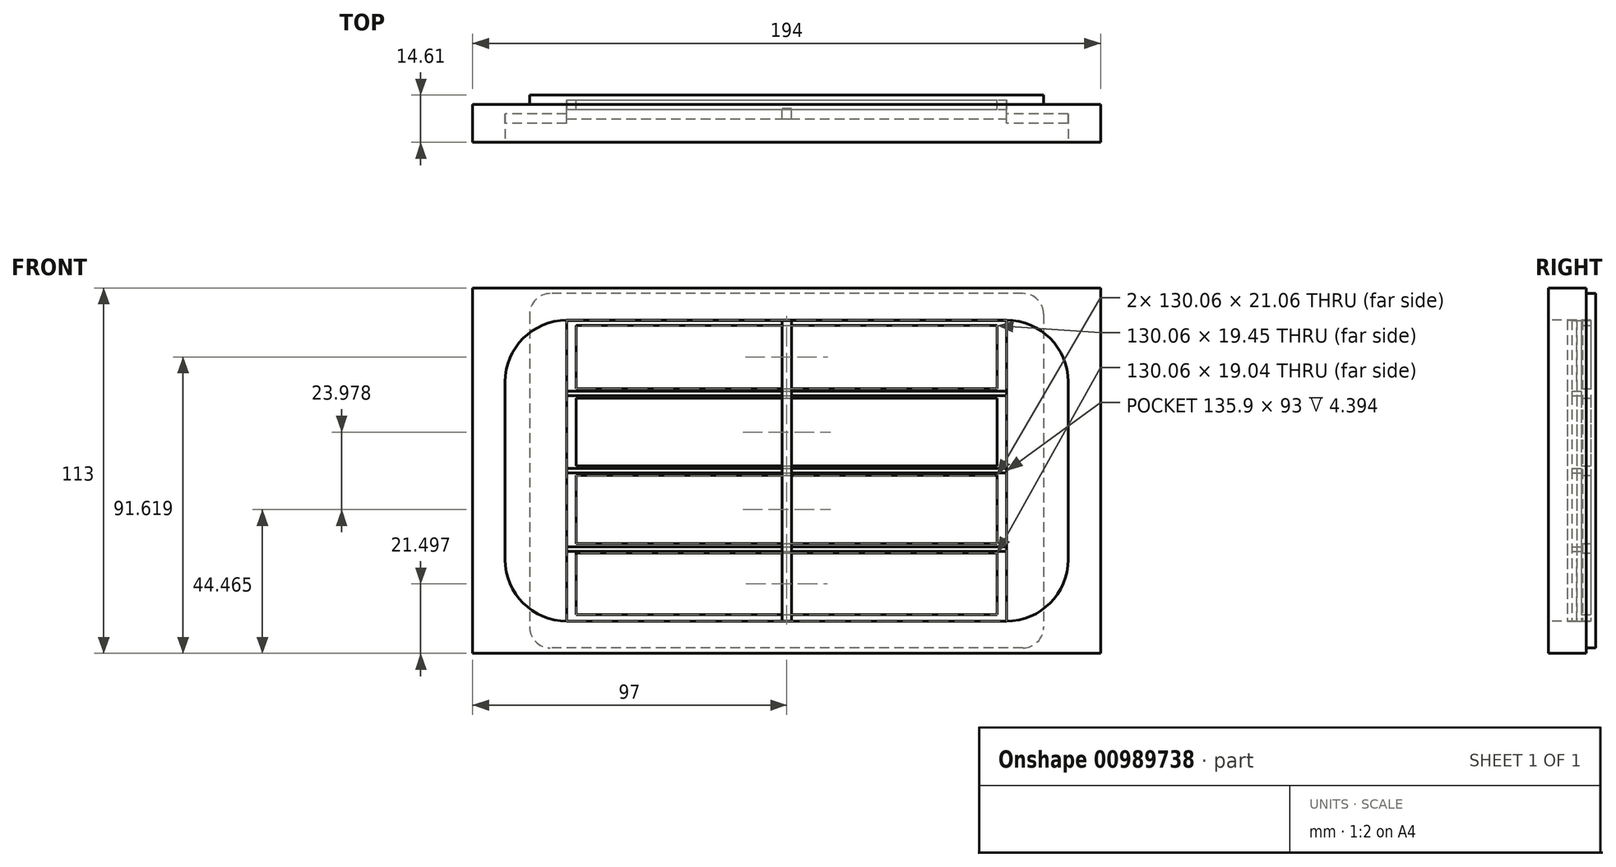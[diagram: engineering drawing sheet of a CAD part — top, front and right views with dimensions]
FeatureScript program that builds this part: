
annotation { "Feature Type Name" : "Feature", "Feature Type Description" : "" }
export const myFeature = defineFeature(function(context is Context, id is Id, definition is map)
    precondition{}
    {
        {
            var Q0;
            Q0=qCreatedBy(makeId("Front.planeOp"),FACE);
            var sketch = newSketch(context, id + "F0", { "sketchPlane" : qUnion([Q0])});
            skLineSegment(sketch, "E0.bottom", {"start": v(73.03, 54.77) * mm, "end": v(-73.03, 54.77) * mm});
            skLineSegment(sketch, "E0.top", {"start": v(73.03, -54.77) * mm, "end": v(-73.02, -54.77) * mm});
            skLineSegment(sketch, "E0.left", {"start": v(79.38, 48.42) * mm, "end": v(79.38, -48.42) * mm});
            skLineSegment(sketch, "E0.right", {"start": v(-79.38, 48.42) * mm, "end": v(-79.37, -48.42) * mm});
            skPoint(sketch, "E0.middle", {"position": v(0, 0) * mm});
            skPoint(sketch, "E1.visualSharp", {"position": v(-79.37, -54.77) * mm});
            skArc(sketch, "E1.filletArc", {"start": v(-79.37, -48.42) * mm, "mid": v(-77.52, -52.9) * mm, "end": v(-73.02, -54.77) * mm});
            skPoint(sketch, "E2.visualSharp", {"position": v(79.38, -54.77) * mm});
            skArc(sketch, "E2.filletArc", {"start": v(73.03, -54.77) * mm, "mid": v(77.52, -52.9) * mm, "end": v(79.38, -48.42) * mm});
            skPoint(sketch, "E3.visualSharp", {"position": v(79.38, 54.77) * mm});
            skArc(sketch, "E3.filletArc", {"start": v(79.38, 48.42) * mm, "mid": v(77.52, 52.9) * mm, "end": v(73.03, 54.77) * mm});
            skPoint(sketch, "E4.visualSharp", {"position": v(-79.38, 54.77) * mm});
            skArc(sketch, "E4.filletArc", {"start": v(-73.03, 54.77) * mm, "mid": v(-77.52, 52.9) * mm, "end": v(-79.38, 48.42) * mm});
            skSolve(sketch);
        }
        {
            var Q0;
            Q0=qSketchRegion(id+"F0",true);
            extrude(context, id + "F1", {"entities" : qUnion([Q0]), "depth" : 2.92 * mm, "offsetDistance" : 25.4 * mm});
        }
        {
            var Q0;
            Q0=makeQuery(id+"F1.opExtrude","CAP_FACE",FACE,{"disambiguationData":[OSD([sQuery(id+"F0.wireOp",EDGE,"E0.bottom"),sQuery(id+"F0.wireOp",EDGE,"E0.top"),sQuery(id+"F0.wireOp",EDGE,"E0.left"),sQuery(id+"F0.wireOp",EDGE,"E0.right")])],"isStart":false});
            var sketch = newSketch(context, id + "F2", { "sketchPlane" : qUnion([Q0])});
            skLineSegment(sketch, "E5.bottom", {"start": v(-97, 56.5) * mm, "end": v(97, 56.5) * mm});
            skLineSegment(sketch, "E5.top", {"start": v(-97, -56.5) * mm, "end": v(97, -56.5) * mm});
            skLineSegment(sketch, "E5.left", {"start": v(-97, 56.5) * mm, "end": v(-97, -56.5) * mm});
            skLineSegment(sketch, "E5.right", {"start": v(97, 56.5) * mm, "end": v(97, -56.5) * mm});
            skPoint(sketch, "E5.middle", {"position": v(0, 0) * mm});
            skSolve(sketch);
        }
        {
            var Q0;
            Q0=qSketchRegion(id+"F2",true);
            extrude(context, id + "F3", {"entities" : qUnion([Q0]), "operationType" : NewBodyOperationType.ADD, "depth" : 11.68 * mm, "offsetDistance" : 25.4 * mm});
        }
        {
            var Q0;
            Q0=makeQuery(id+"F3.opExtrude","CAP_FACE",FACE,{"disambiguationData":[OSD([sQuery(id+"F2.wireOp",EDGE,"E5.bottom"),sQuery(id+"F2.wireOp",EDGE,"E5.top"),sQuery(id+"F2.wireOp",EDGE,"E5.left"),sQuery(id+"F2.wireOp",EDGE,"E5.right")])],"isStart":false});
            var sketch = newSketch(context, id + "F4", { "sketchPlane" : qUnion([Q0])});
            skLineSegment(sketch, "E6.bottom", {"start": v(-67.95, 46.5) * mm, "end": v(67.95, 46.5) * mm});
            skLineSegment(sketch, "E6.top", {"start": v(-67.95, -46.5) * mm, "end": v(67.95, -46.5) * mm});
            skLineSegment(sketch, "E6.left", {"start": v(-87, 27.45) * mm, "end": v(-87, -27.45) * mm});
            skLineSegment(sketch, "E6.right", {"start": v(87, 27.45) * mm, "end": v(87, -27.45) * mm});
            skPoint(sketch, "E6.middle", {"position": v(0, 0) * mm});
            skPoint(sketch, "E7.visualSharp", {"position": v(-87, 46.5) * mm});
            skArc(sketch, "E7.filletArc", {"start": v(-67.95, 46.5) * mm, "mid": v(-81.42, 40.92) * mm, "end": v(-87, 27.45) * mm});
            skPoint(sketch, "E8.visualSharp", {"position": v(87, 46.5) * mm});
            skArc(sketch, "E8.filletArc", {"start": v(87, 27.45) * mm, "mid": v(81.42, 40.92) * mm, "end": v(67.95, 46.5) * mm});
            skPoint(sketch, "E9.visualSharp", {"position": v(87, -46.5) * mm});
            skArc(sketch, "E9.filletArc", {"start": v(67.95, -46.5) * mm, "mid": v(81.42, -40.92) * mm, "end": v(87, -27.45) * mm});
            skPoint(sketch, "E10.visualSharp", {"position": v(-87, -46.5) * mm});
            skArc(sketch, "E10.filletArc", {"start": v(-87, -27.45) * mm, "mid": v(-81.42, -40.92) * mm, "end": v(-67.95, -46.5) * mm});
            skSolve(sketch);
        }
        {
            var Q0;
            Q0=makeQuery(id+"F4.imprint","IMPRINT",FACE,{"disambiguationData":[TD([[makeQuery(id+"F4.imprint","IMPRINT",EDGE,{"derivedFrom":sQuery(id+"F4.wireOp",EDGE,"E6.bottom")}),-1.0]])]});
            extrude(context, id + "F5", {"entities" : qUnion([Q0]), "operationType" : NewBodyOperationType.REMOVE, "oppositeDirection" : true, "depth" : 8.76 * mm, "offsetDistance" : 25.4 * mm});
        }
        {
            var Q0;
            Q0=makeQuery(id+"F5.boolean.opBoolean","COPY",FACE,{"derivedFrom":makeQuery(id+"F5.opExtrude","CAP_FACE",FACE,{"disambiguationData":[OSD([sQuery(id+"F4.wireOp",EDGE,"E6.bottom"),sQuery(id+"F4.wireOp",EDGE,"E6.top"),sQuery(id+"F4.wireOp",EDGE,"E6.left"),sQuery(id+"F4.wireOp",EDGE,"E6.right"),sQuery(id+"F4.wireOp",EDGE,"E7.filletArc"),sQuery(id+"F4.wireOp",EDGE,"E8.filletArc"),sQuery(id+"F4.wireOp",EDGE,"E9.filletArc"),sQuery(id+"F4.wireOp",EDGE,"E10.filletArc")])],"isStart":false})});
            var sketch = newSketch(context, id + "F6", { "sketchPlane" : qUnion([Q0])});
            skLineSegment(sketch, "E11.bottom", {"start": v(-67.95, 46.5) * mm, "end": v(67.95, 46.5) * mm});
            skLineSegment(sketch, "E11.top", {"start": v(-67.95, -46.5) * mm, "end": v(67.95, -46.5) * mm});
            skLineSegment(sketch, "E11.left", {"start": v(-67.95, 46.5) * mm, "end": v(-67.95, -46.5) * mm});
            skLineSegment(sketch, "E11.right", {"start": v(67.95, 46.5) * mm, "end": v(67.95, -46.5) * mm});
            skSolve(sketch);
        }
        {
            var Q0;
            Q0=makeQuery(id+"F6.imprint","IMPRINT",FACE,{"disambiguationData":[TD([[makeQuery(id+"F6.imprint","IMPRINT",EDGE,{"derivedFrom":sQuery(id+"F6.wireOp",EDGE,"E11.bottom")}),-1.0]])]});
            extrude(context, id + "F7", {"entities" : qUnion([Q0]), "operationType" : NewBodyOperationType.REMOVE, "oppositeDirection" : true, "depth" : 4.4 * mm, "offsetDistance" : 25.4 * mm});
        }
        {
            var Q0;
            Q0=qCreatedBy(makeId("Front.planeOp"),FACE);
            cPlane(context, id + "F8", {"entities" : qUnion([Q0]), "cplaneType" : CPlaneType.OFFSET, "offset" : 4 * mm, "width" : 152.4 * mm, "height" : 152.4 * mm});
        }
        {
            var Q0;
            Q0=qCreatedBy(id+"F8.planeOp",FACE);
            var sketch = newSketch(context, id + "F9", { "sketchPlane" : qUnion([Q0])});
            skLineSegment(sketch, "E12.bottom", {"start": v(-1.46, 46.45) * mm, "end": v(1.46, 46.45) * mm});
            skLineSegment(sketch, "E12.top", {"start": v(-1.46, -46.55) * mm, "end": v(1.46, -46.55) * mm});
            skLineSegment(sketch, "E12.left", {"start": v(-1.46, 46.45) * mm, "end": v(-1.46, -46.55) * mm});
            skLineSegment(sketch, "E12.right", {"start": v(1.46, 46.45) * mm, "end": v(1.46, -46.55) * mm});
            skPoint(sketch, "E12.middle", {"position": v(0, -0.05) * mm});
            skLineSegment(sketch, "E13.bottom", {"start": v(-67.95, 46.45) * mm, "end": v(-65.03, 46.45) * mm});
            skLineSegment(sketch, "E13.top", {"start": v(-67.95, -46.55) * mm, "end": v(-65.03, -46.55) * mm});
            skLineSegment(sketch, "E13.left", {"start": v(-67.95, 46.45) * mm, "end": v(-67.95, -46.55) * mm});
            skLineSegment(sketch, "E13.right", {"start": v(-65.03, 46.45) * mm, "end": v(-65.03, -46.55) * mm});
            skLineSegment(sketch, "E14.bottom", {"start": v(67.95, 47.77) * mm, "end": v(65.03, 47.77) * mm});
            skLineSegment(sketch, "E14.top", {"start": v(67.95, -47.44) * mm, "end": v(65.03, -47.44) * mm});
            skLineSegment(sketch, "E14.left", {"start": v(67.95, 47.77) * mm, "end": v(67.95, -47.44) * mm});
            skLineSegment(sketch, "E14.right", {"start": v(65.03, 47.77) * mm, "end": v(65.03, -47.44) * mm});
            skLineSegment(sketch, "E15.bottom", {"start": v(-65.03, 1.41) * mm, "end": v(65.03, 1.41) * mm});
            skLineSegment(sketch, "E15.top", {"start": v(-65.03, -1.5) * mm, "end": v(65.03, -1.5) * mm});
            skLineSegment(sketch, "E15.left", {"start": v(-65.03, 1.41) * mm, "end": v(-65.03, -1.5) * mm});
            skLineSegment(sketch, "E15.right", {"start": v(65.03, 1.41) * mm, "end": v(65.03, -1.5) * mm});
            skLineSegment(sketch, "E16.bottom", {"start": v(-65.03, 25.4) * mm, "end": v(65.03, 25.4) * mm});
            skLineSegment(sketch, "E16.top", {"start": v(-65.03, 22.47) * mm, "end": v(65.03, 22.47) * mm});
            skLineSegment(sketch, "E16.left", {"start": v(-65.03, 25.4) * mm, "end": v(-65.03, 22.47) * mm});
            skLineSegment(sketch, "E16.right", {"start": v(65.03, 25.4) * mm, "end": v(65.03, 22.47) * mm});
            skPoint(sketch, "E16.middle", {"position": v(0, 23.93) * mm});
            skLineSegment(sketch, "E17.bottom", {"start": v(-65.03, -25.48) * mm, "end": v(65.03, -25.48) * mm});
            skLineSegment(sketch, "E17.top", {"start": v(-65.03, -22.56) * mm, "end": v(65.03, -22.56) * mm});
            skLineSegment(sketch, "E17.left", {"start": v(-65.03, -25.48) * mm, "end": v(-65.03, -22.56) * mm});
            skLineSegment(sketch, "E17.right", {"start": v(65.03, -25.48) * mm, "end": v(65.03, -22.56) * mm});
            skPoint(sketch, "E17.middle", {"position": v(0, -24.02) * mm});
            skLineSegment(sketch, "E18.bottom", {"start": v(-67.95, -46.55) * mm, "end": v(67.95, -46.55) * mm});
            skLineSegment(sketch, "E18.top", {"start": v(-67.95, -44.52) * mm, "end": v(67.95, -44.52) * mm});
            skLineSegment(sketch, "E18.left", {"start": v(-67.95, -46.55) * mm, "end": v(-67.95, -44.52) * mm});
            skLineSegment(sketch, "E18.right", {"start": v(67.95, -46.55) * mm, "end": v(67.95, -44.52) * mm});
            skLineSegment(sketch, "E19.bottom", {"start": v(-67.95, 46.45) * mm, "end": v(67.95, 46.45) * mm});
            skLineSegment(sketch, "E19.top", {"start": v(-67.95, 44.85) * mm, "end": v(67.95, 44.85) * mm});
            skLineSegment(sketch, "E19.left", {"start": v(-67.95, 46.45) * mm, "end": v(-67.95, 44.85) * mm});
            skLineSegment(sketch, "E19.right", {"start": v(67.95, 46.45) * mm, "end": v(67.95, 44.85) * mm});
            skSolve(sketch);
        }
        {
            var Q0;
            {var subQ0=sQuery(id+"F9.wireOp",EDGE,"E19.top");var subQ1=sQuery(id+"F9.wireOp",EDGE,"E12.left");var subQ2=makeQuery(id+"F9.imprint","INTERSECT",VERTEX,{"derivedFrom":[subQ1,subQ0]});Q0=makeQuery(id+"F9.imprint","IMPRINT",FACE,{"disambiguationData":[TD([[makeQuery(id+"F9.imprint","IMPRINT",EDGE,{"disambiguationData":[TD([[subQ2,-1.0]])],"derivedFrom":subQ1}),1.0]])]});}
            var Q1;
            {var subQ0=sQuery(id+"F9.wireOp",EDGE,"E16.top");var subQ1=sQuery(id+"F9.wireOp",EDGE,"E12.left");var subQ2=makeQuery(id+"F9.imprint","INTERSECT",VERTEX,{"derivedFrom":[subQ1,subQ0]});Q1=makeQuery(id+"F9.imprint","IMPRINT",FACE,{"disambiguationData":[TD([[makeQuery(id+"F9.imprint","IMPRINT",EDGE,{"disambiguationData":[TD([[subQ2,-1.0]])],"derivedFrom":subQ1}),1.0]])]});}
            var Q2;
            {var subQ0=sQuery(id+"F9.wireOp",EDGE,"E15.top");var subQ1=sQuery(id+"F9.wireOp",EDGE,"E12.left");var subQ2=makeQuery(id+"F9.imprint","INTERSECT",VERTEX,{"derivedFrom":[subQ1,subQ0]});Q2=makeQuery(id+"F9.imprint","IMPRINT",FACE,{"disambiguationData":[TD([[makeQuery(id+"F9.imprint","IMPRINT",EDGE,{"disambiguationData":[TD([[subQ2,-1.0]])],"derivedFrom":subQ1}),1.0]])]});}
            var Q3;
            {var subQ0=sQuery(id+"F9.wireOp",EDGE,"E17.bottom");var subQ1=sQuery(id+"F9.wireOp",EDGE,"E12.left");var subQ2=makeQuery(id+"F9.imprint","INTERSECT",VERTEX,{"derivedFrom":[subQ1,subQ0]});Q3=makeQuery(id+"F9.imprint","IMPRINT",FACE,{"disambiguationData":[TD([[makeQuery(id+"F9.imprint","IMPRINT",EDGE,{"disambiguationData":[TD([[subQ2,-1.0]])],"derivedFrom":subQ1}),1.0]])]});}
            var Q4;
            {var subQ0=sQuery(id+"F9.wireOp",EDGE,"E16.bottom");var subQ1=sQuery(id+"F9.wireOp",EDGE,"E12.left");var subQ2=makeQuery(id+"F9.imprint","INTERSECT",VERTEX,{"derivedFrom":[subQ1,subQ0]});Q4=makeQuery(id+"F9.imprint","IMPRINT",FACE,{"disambiguationData":[TD([[makeQuery(id+"F9.imprint","IMPRINT",EDGE,{"disambiguationData":[TD([[subQ2,-1.0]])],"derivedFrom":subQ1}),1.0]])]});}
            var Q5;
            {var subQ0=sQuery(id+"F9.wireOp",EDGE,"E15.bottom");var subQ1=sQuery(id+"F9.wireOp",EDGE,"E12.left");var subQ2=makeQuery(id+"F9.imprint","INTERSECT",VERTEX,{"derivedFrom":[subQ1,subQ0]});Q5=makeQuery(id+"F9.imprint","IMPRINT",FACE,{"disambiguationData":[TD([[makeQuery(id+"F9.imprint","IMPRINT",EDGE,{"disambiguationData":[TD([[subQ2,-1.0]])],"derivedFrom":subQ1}),1.0]])]});}
            var Q6;
            {var subQ0=sQuery(id+"F9.wireOp",EDGE,"E17.top");var subQ1=sQuery(id+"F9.wireOp",EDGE,"E12.left");var subQ2=makeQuery(id+"F9.imprint","INTERSECT",VERTEX,{"derivedFrom":[subQ1,subQ0]});Q6=makeQuery(id+"F9.imprint","IMPRINT",FACE,{"disambiguationData":[TD([[makeQuery(id+"F9.imprint","IMPRINT",EDGE,{"disambiguationData":[TD([[subQ2,-1.0]])],"derivedFrom":subQ1}),1.0]])]});}
            var Q7;
            {var subQ0=sQuery(id+"F9.wireOp",EDGE,"E19.bottom");var subQ1=sQuery(id+"F9.wireOp",EDGE,"E12.left");var subQ2=makeQuery(id+"F9.imprint","INTERSECT",VERTEX,{"derivedFrom":[subQ1,subQ0]});Q7=makeQuery(id+"F9.imprint","IMPRINT",FACE,{"disambiguationData":[TD([[makeQuery(id+"F9.imprint","IMPRINT",EDGE,{"disambiguationData":[TD([[subQ2,-1.0]])],"derivedFrom":subQ1}),1.0]])]});}
            var Q8;
            {var subQ0=sQuery(id+"F9.wireOp",EDGE,"E18.bottom");var subQ1=sQuery(id+"F9.wireOp",EDGE,"E12.left");var subQ2=makeQuery(id+"F9.imprint","INTERSECT",VERTEX,{"derivedFrom":[subQ1,subQ0]});Q8=makeQuery(id+"F9.imprint","IMPRINT",FACE,{"disambiguationData":[TD([[makeQuery(id+"F9.imprint","IMPRINT",EDGE,{"disambiguationData":[TD([[subQ2,1.0]])],"derivedFrom":subQ1}),1.0]])]});}
            extrude(context, id + "F10", {"entities" : qUnion([Q0, Q1, Q2, Q3, Q4, Q5, Q6, Q7, Q8]), "depth" : 3.31 * mm, "offsetDistance" : 25.4 * mm});
        }
        {
            var Q0;
            Q0=makeQuery(id+"F7.boolean.opBoolean","COPY",FACE,{"derivedFrom":makeQuery(id+"F7.opExtrude","CAP_FACE",FACE,{"disambiguationData":[OSD([sQuery(id+"F6.wireOp",EDGE,"E11.bottom"),sQuery(id+"F6.wireOp",EDGE,"E11.top"),sQuery(id+"F6.wireOp",EDGE,"E11.left"),sQuery(id+"F6.wireOp",EDGE,"E11.right")])],"isStart":false})});
            var sketch = newSketch(context, id + "F11", { "sketchPlane" : qUnion([Q0])});
            skLineSegment(sketch, "E20.bottom", {"start": v(-1.46, 46.45) * mm, "end": v(1.46, 46.45) * mm});
            skLineSegment(sketch, "E20.top", {"start": v(-1.46, -46.55) * mm, "end": v(1.46, -46.55) * mm});
            skLineSegment(sketch, "E20.left", {"start": v(-1.46, 46.45) * mm, "end": v(-1.46, -46.55) * mm});
            skLineSegment(sketch, "E20.right", {"start": v(1.46, 46.45) * mm, "end": v(1.46, -46.55) * mm});
            skPoint(sketch, "E20.middle", {"position": v(0, -0.05) * mm});
            skLineSegment(sketch, "E21.bottom", {"start": v(-67.95, 46.45) * mm, "end": v(-65.03, 46.45) * mm});
            skLineSegment(sketch, "E21.top", {"start": v(-67.95, -46.55) * mm, "end": v(-65.03, -46.55) * mm});
            skLineSegment(sketch, "E21.left", {"start": v(-67.95, 46.45) * mm, "end": v(-67.95, -46.55) * mm});
            skLineSegment(sketch, "E21.right", {"start": v(-65.03, 46.45) * mm, "end": v(-65.03, -46.55) * mm});
            skLineSegment(sketch, "E22.bottom", {"start": v(67.95, 47.77) * mm, "end": v(65.03, 47.77) * mm});
            skLineSegment(sketch, "E22.top", {"start": v(67.95, -47.44) * mm, "end": v(65.03, -47.44) * mm});
            skLineSegment(sketch, "E22.left", {"start": v(67.95, 47.77) * mm, "end": v(67.95, -47.44) * mm});
            skLineSegment(sketch, "E22.right", {"start": v(65.03, 47.77) * mm, "end": v(65.03, -47.44) * mm});
            skLineSegment(sketch, "E23.bottom", {"start": v(-65.03, 1.41) * mm, "end": v(65.03, 1.41) * mm});
            skLineSegment(sketch, "E23.top", {"start": v(-65.03, -1.5) * mm, "end": v(65.03, -1.5) * mm});
            skLineSegment(sketch, "E23.left", {"start": v(-65.03, 1.41) * mm, "end": v(-65.03, -1.5) * mm});
            skLineSegment(sketch, "E23.right", {"start": v(65.03, 1.41) * mm, "end": v(65.03, -1.5) * mm});
            skLineSegment(sketch, "E24.bottom", {"start": v(-65.03, 25.4) * mm, "end": v(65.03, 25.4) * mm});
            skLineSegment(sketch, "E24.top", {"start": v(-65.03, 22.47) * mm, "end": v(65.03, 22.47) * mm});
            skLineSegment(sketch, "E24.left", {"start": v(-65.03, 25.4) * mm, "end": v(-65.03, 22.47) * mm});
            skLineSegment(sketch, "E24.right", {"start": v(65.03, 25.4) * mm, "end": v(65.03, 22.47) * mm});
            skPoint(sketch, "E24.middle", {"position": v(0, 23.93) * mm});
            skLineSegment(sketch, "E25.bottom", {"start": v(-65.03, -25.48) * mm, "end": v(65.03, -25.48) * mm});
            skLineSegment(sketch, "E25.top", {"start": v(-65.03, -22.56) * mm, "end": v(65.03, -22.56) * mm});
            skLineSegment(sketch, "E25.left", {"start": v(-65.03, -25.48) * mm, "end": v(-65.03, -22.56) * mm});
            skLineSegment(sketch, "E25.right", {"start": v(65.03, -25.48) * mm, "end": v(65.03, -22.56) * mm});
            skPoint(sketch, "E25.middle", {"position": v(0, -24.02) * mm});
            skLineSegment(sketch, "E26.bottom", {"start": v(-67.95, -46.55) * mm, "end": v(67.95, -46.55) * mm});
            skLineSegment(sketch, "E26.top", {"start": v(-67.95, -44.52) * mm, "end": v(67.95, -44.52) * mm});
            skLineSegment(sketch, "E26.left", {"start": v(-67.95, -46.55) * mm, "end": v(-67.95, -44.52) * mm});
            skLineSegment(sketch, "E26.right", {"start": v(67.95, -46.55) * mm, "end": v(67.95, -44.52) * mm});
            skLineSegment(sketch, "E27.bottom", {"start": v(-67.95, 46.45) * mm, "end": v(67.95, 46.45) * mm});
            skLineSegment(sketch, "E27.top", {"start": v(-67.95, 44.85) * mm, "end": v(67.95, 44.85) * mm});
            skLineSegment(sketch, "E27.left", {"start": v(-67.95, 46.45) * mm, "end": v(-67.95, 44.85) * mm});
            skLineSegment(sketch, "E27.right", {"start": v(67.95, 46.45) * mm, "end": v(67.95, 44.85) * mm});
            skSolve(sketch);
        }
        {
            var Q0;
            {var subQ0=sQuery(id+"F11.wireOp",EDGE,"E24.top");var subQ1=sQuery(id+"F11.wireOp",EDGE,"E20.left");var subQ2=makeQuery(id+"F11.imprint","INTERSECT",VERTEX,{"derivedFrom":[subQ1,subQ0]});Q0=makeQuery(id+"F11.imprint","IMPRINT",FACE,{"disambiguationData":[TD([[makeQuery(id+"F11.imprint","IMPRINT",EDGE,{"disambiguationData":[TD([[subQ2,1.0]])],"derivedFrom":subQ1}),-1.0]])]});}
            var Q1;
            {var subQ0=sQuery(id+"F11.wireOp",EDGE,"E23.bottom");var subQ1=sQuery(id+"F11.wireOp",EDGE,"E20.left");var subQ2=makeQuery(id+"F11.imprint","INTERSECT",VERTEX,{"derivedFrom":[subQ1,subQ0]});Q1=makeQuery(id+"F11.imprint","IMPRINT",FACE,{"disambiguationData":[TD([[makeQuery(id+"F11.imprint","IMPRINT",EDGE,{"disambiguationData":[TD([[subQ2,-1.0]])],"derivedFrom":subQ1}),-1.0]])]});}
            var Q2;
            {var subQ0=sQuery(id+"F11.wireOp",EDGE,"E25.top");var subQ1=sQuery(id+"F11.wireOp",EDGE,"E20.left");var subQ2=makeQuery(id+"F11.imprint","INTERSECT",VERTEX,{"derivedFrom":[subQ1,subQ0]});Q2=makeQuery(id+"F11.imprint","IMPRINT",FACE,{"disambiguationData":[TD([[makeQuery(id+"F11.imprint","IMPRINT",EDGE,{"disambiguationData":[TD([[subQ2,-1.0]])],"derivedFrom":subQ1}),-1.0]])]});}
            var Q3;
            {var subQ0=sQuery(id+"F11.wireOp",EDGE,"E26.top");var subQ1=sQuery(id+"F11.wireOp",EDGE,"E20.left");var subQ2=makeQuery(id+"F11.imprint","INTERSECT",VERTEX,{"derivedFrom":[subQ1,subQ0]});Q3=makeQuery(id+"F11.imprint","IMPRINT",FACE,{"disambiguationData":[TD([[makeQuery(id+"F11.imprint","IMPRINT",EDGE,{"disambiguationData":[TD([[subQ2,-1.0]])],"derivedFrom":subQ1}),-1.0]])]});}
            var Q4;
            {var subQ0=sQuery(id+"F11.wireOp",EDGE,"E21.left");var subQ1=makeQuery(id+"F7.boolean.opBoolean","COPY",EDGE,{"derivedFrom":makeQuery(id+"F7.opExtrude","CAP_EDGE",EDGE,{"disambiguationData":[OSD([sQuery(id+"F6.wireOp",EDGE,"E11.top")])],"isStart":false})});var subQ2=makeQuery(id+"F11.imprint","INTERSECT",VERTEX,{"derivedFrom":[subQ1,subQ0]});Q4=makeQuery(id+"F11.imprint","IMPRINT",FACE,{"disambiguationData":[TD([[makeQuery(id+"F11.imprint","IMPRINT",EDGE,{"disambiguationData":[TD([[subQ2,1.0]])],"derivedFrom":subQ0}),1.0]])]});}
            var Q5;
            {var subQ0=sQuery(id+"F11.wireOp",EDGE,"E26.top");var subQ1=sQuery(id+"F11.wireOp",EDGE,"E20.left");var subQ2=makeQuery(id+"F11.imprint","INTERSECT",VERTEX,{"derivedFrom":[subQ1,subQ0]});Q5=makeQuery(id+"F11.imprint","IMPRINT",FACE,{"disambiguationData":[TD([[makeQuery(id+"F11.imprint","IMPRINT",EDGE,{"disambiguationData":[TD([[subQ2,-1.0]])],"derivedFrom":subQ1}),1.0]])]});}
            var Q6;
            {var subQ0=sQuery(id+"F11.wireOp",EDGE,"E26.top");var subQ1=sQuery(id+"F11.wireOp",EDGE,"E20.right");var subQ2=makeQuery(id+"F11.imprint","INTERSECT",VERTEX,{"derivedFrom":[subQ1,subQ0]});Q6=makeQuery(id+"F11.imprint","IMPRINT",FACE,{"disambiguationData":[TD([[makeQuery(id+"F11.imprint","IMPRINT",EDGE,{"disambiguationData":[TD([[subQ2,-1.0]])],"derivedFrom":subQ1}),1.0]])]});}
            var Q7;
            {var subQ0=sQuery(id+"F11.wireOp",EDGE,"E25.bottom");var subQ1=sQuery(id+"F11.wireOp",EDGE,"E20.right");var subQ2=makeQuery(id+"F11.imprint","INTERSECT",VERTEX,{"derivedFrom":[subQ1,subQ0]});Q7=makeQuery(id+"F11.imprint","IMPRINT",FACE,{"disambiguationData":[TD([[makeQuery(id+"F11.imprint","IMPRINT",EDGE,{"disambiguationData":[TD([[subQ2,1.0]])],"derivedFrom":subQ1}),1.0]])]});}
            var Q8;
            {var subQ0=sQuery(id+"F11.wireOp",EDGE,"E23.bottom");var subQ1=sQuery(id+"F11.wireOp",EDGE,"E20.right");var subQ2=makeQuery(id+"F11.imprint","INTERSECT",VERTEX,{"derivedFrom":[subQ1,subQ0]});Q8=makeQuery(id+"F11.imprint","IMPRINT",FACE,{"disambiguationData":[TD([[makeQuery(id+"F11.imprint","IMPRINT",EDGE,{"disambiguationData":[TD([[subQ2,-1.0]])],"derivedFrom":subQ1}),1.0]])]});}
            var Q9;
            {var subQ0=sQuery(id+"F11.wireOp",EDGE,"E24.top");var subQ1=sQuery(id+"F11.wireOp",EDGE,"E20.right");var subQ2=makeQuery(id+"F11.imprint","INTERSECT",VERTEX,{"derivedFrom":[subQ1,subQ0]});Q9=makeQuery(id+"F11.imprint","IMPRINT",FACE,{"disambiguationData":[TD([[makeQuery(id+"F11.imprint","IMPRINT",EDGE,{"disambiguationData":[TD([[subQ2,1.0]])],"derivedFrom":subQ1}),1.0]])]});}
            var Q10;
            {var subQ4=sQuery(id+"F11.wireOp",EDGE,"E22.left");var subQ10=sQuery(id+"F11.wireOp",EDGE,"E26.top");var subQ11=makeQuery(id+"F11.imprint","INTERSECT",VERTEX,{"derivedFrom":[subQ4,subQ10]});Q10=makeQuery(id+"F11.imprint","IMPRINT",FACE,{"disambiguationData":[TD([[makeQuery(id+"F11.imprint","IMPRINT",EDGE,{"disambiguationData":[TD([[subQ11,1.0]])],"derivedFrom":subQ4}),-1.0]])]});}
            var Q11;
            {var subQ3=sQuery(id+"F11.wireOp",EDGE,"E27.top");var subQ5=sQuery(id+"F11.wireOp",EDGE,"E22.right");var subQ6=makeQuery(id+"F11.imprint","INTERSECT",VERTEX,{"derivedFrom":[subQ5,subQ3]});Q11=makeQuery(id+"F11.imprint","IMPRINT",FACE,{"disambiguationData":[TD([[makeQuery(id+"F11.imprint","IMPRINT",EDGE,{"disambiguationData":[TD([[subQ6,1.0]])],"derivedFrom":subQ5}),-1.0]])]});}
            var Q12;
            {var subQ1=sQuery(id+"F11.wireOp",EDGE,"E20.left");var subQ3=sQuery(id+"F11.wireOp",EDGE,"E27.top");var subQ4=makeQuery(id+"F11.imprint","INTERSECT",VERTEX,{"derivedFrom":[subQ1,subQ3]});Q12=makeQuery(id+"F11.imprint","IMPRINT",FACE,{"disambiguationData":[TD([[makeQuery(id+"F11.imprint","IMPRINT",EDGE,{"disambiguationData":[TD([[subQ4,1.0]])],"derivedFrom":subQ3}),1.0]])]});}
            var Q13;
            {var subQ0=sQuery(id+"F11.wireOp",EDGE,"E24.top");var subQ1=sQuery(id+"F11.wireOp",EDGE,"E20.left");var subQ2=makeQuery(id+"F11.imprint","INTERSECT",VERTEX,{"derivedFrom":[subQ1,subQ0]});Q13=makeQuery(id+"F11.imprint","IMPRINT",FACE,{"disambiguationData":[TD([[makeQuery(id+"F11.imprint","IMPRINT",EDGE,{"disambiguationData":[TD([[subQ2,1.0]])],"derivedFrom":subQ1}),1.0]])]});}
            var Q14;
            {var subQ0=sQuery(id+"F11.wireOp",EDGE,"E20.bottom");Q14=makeQuery(id+"F11.imprint","IMPRINT",FACE,{"disambiguationData":[TD([[makeQuery(id+"F11.imprint","IMPRINT",EDGE,{"derivedFrom":subQ0}),-1.0]])]});}
            var Q15;
            {var subQ0=sQuery(id+"F11.wireOp",EDGE,"E23.bottom");var subQ1=sQuery(id+"F11.wireOp",EDGE,"E20.left");var subQ2=makeQuery(id+"F11.imprint","INTERSECT",VERTEX,{"derivedFrom":[subQ1,subQ0]});Q15=makeQuery(id+"F11.imprint","IMPRINT",FACE,{"disambiguationData":[TD([[makeQuery(id+"F11.imprint","IMPRINT",EDGE,{"disambiguationData":[TD([[subQ2,-1.0]])],"derivedFrom":subQ1}),1.0]])]});}
            var Q16;
            {var subQ0=sQuery(id+"F11.wireOp",EDGE,"E25.top");var subQ1=sQuery(id+"F11.wireOp",EDGE,"E20.left");var subQ2=makeQuery(id+"F11.imprint","INTERSECT",VERTEX,{"derivedFrom":[subQ1,subQ0]});Q16=makeQuery(id+"F11.imprint","IMPRINT",FACE,{"disambiguationData":[TD([[makeQuery(id+"F11.imprint","IMPRINT",EDGE,{"disambiguationData":[TD([[subQ2,-1.0]])],"derivedFrom":subQ1}),1.0]])]});}
            var Q17;
            {var subQ0=sQuery(id+"F11.wireOp",EDGE,"E22.left");var subQ1=makeQuery(id+"F7.boolean.opBoolean","COPY",EDGE,{"derivedFrom":makeQuery(id+"F7.opExtrude","CAP_EDGE",EDGE,{"disambiguationData":[OSD([sQuery(id+"F6.wireOp",EDGE,"E11.top")])],"isStart":false})});var subQ2=makeQuery(id+"F11.imprint","INTERSECT",VERTEX,{"derivedFrom":[subQ1,subQ0]});Q17=makeQuery(id+"F11.imprint","IMPRINT",FACE,{"disambiguationData":[TD([[makeQuery(id+"F11.imprint","IMPRINT",EDGE,{"disambiguationData":[TD([[subQ2,1.0]])],"derivedFrom":subQ0}),-1.0]])]});}
            var Q18;
            {var subQ0=sQuery(id+"F11.wireOp",EDGE,"E27.bottom");var subQ1=sQuery(id+"F11.wireOp",EDGE,"E22.left");var subQ2=makeQuery(id+"F11.imprint","INTERSECT",VERTEX,{"derivedFrom":[subQ1,subQ0]});Q18=makeQuery(id+"F11.imprint","IMPRINT",FACE,{"disambiguationData":[TD([[makeQuery(id+"F11.imprint","IMPRINT",EDGE,{"disambiguationData":[TD([[subQ2,-1.0]])],"derivedFrom":subQ1}),-1.0]])]});}
            var Q19;
            {var subQ0=sQuery(id+"F11.wireOp",EDGE,"E21.bottom");Q19=makeQuery(id+"F11.imprint","IMPRINT",FACE,{"disambiguationData":[TD([[makeQuery(id+"F11.imprint","IMPRINT",EDGE,{"derivedFrom":subQ0}),-1.0]])]});}
            var Q20;
            {var subQ6=sQuery(id+"F11.wireOp",EDGE,"E21.left");var subQ10=sQuery(id+"F11.wireOp",EDGE,"E27.top");var subQ12=makeQuery(id+"F11.imprint","INTERSECT",VERTEX,{"derivedFrom":[subQ6,subQ10]});Q20=makeQuery(id+"F11.imprint","IMPRINT",FACE,{"disambiguationData":[TD([[makeQuery(id+"F11.imprint","IMPRINT",EDGE,{"disambiguationData":[TD([[subQ12,-1.0]])],"derivedFrom":subQ6}),1.0]])]});}
            extrude(context, id + "F12", {"entities" : qUnion([Q0, Q1, Q2, Q3, Q4, Q5, Q6, Q7, Q8, Q9, Q10, Q11, Q12, Q13, Q14, Q15, Q16, Q17, Q18, Q19, Q20]), "depth" : 2.92 * mm, "offsetDistance" : 25.4 * mm});
        }
        {
            var Q0;
            Q0=makeQuery(id+"F12.opExtrude","CAP_FACE",FACE,{"disambiguationData":[OSD([sQuery(id+"F6.wireOp",EDGE,"E11.top"),sQuery(id+"F11.wireOp",EDGE,"E20.bottom"),sQuery(id+"F11.wireOp",EDGE,"E21.bottom"),sQuery(id+"F11.wireOp",EDGE,"E21.left"),sQuery(id+"F11.wireOp",EDGE,"E21.right"),sQuery(id+"F11.wireOp",EDGE,"E22.left"),sQuery(id+"F11.wireOp",EDGE,"E22.right"),sQuery(id+"F11.wireOp",EDGE,"E23.bottom"),sQuery(id+"F11.wireOp",EDGE,"E23.top"),sQuery(id+"F11.wireOp",EDGE,"E24.bottom"),sQuery(id+"F11.wireOp",EDGE,"E24.top"),sQuery(id+"F11.wireOp",EDGE,"E25.bottom"),sQuery(id+"F11.wireOp",EDGE,"E25.top"),sQuery(id+"F11.wireOp",EDGE,"E26.top"),sQuery(id+"F11.wireOp",EDGE,"E27.bottom"),sQuery(id+"F11.wireOp",EDGE,"E27.top")])],"isStart":false});
            var sketch = newSketch(context, id + "F13", { "sketchPlane" : qUnion([Q0])});
            skLineSegment(sketch, "E28.bottom", {"start": v(-67.95, 0.73) * mm, "end": v(67.95, 0.73) * mm});
            skLineSegment(sketch, "E28.top", {"start": v(-67.95, -0.73) * mm, "end": v(67.95, -0.73) * mm});
            skLineSegment(sketch, "E28.left", {"start": v(-67.95, 0.73) * mm, "end": v(-67.95, -0.73) * mm});
            skLineSegment(sketch, "E28.right", {"start": v(67.95, 0.73) * mm, "end": v(67.95, -0.73) * mm});
            skPoint(sketch, "E28.middle", {"position": v(0, 0) * mm});
            skLineSegment(sketch, "E29.bottom", {"start": v(-67.95, 25.4) * mm, "end": v(67.95, 25.4) * mm});
            skLineSegment(sketch, "E29.top", {"start": v(-67.95, 22.47) * mm, "end": v(67.95, 22.47) * mm});
            skLineSegment(sketch, "E29.left", {"start": v(-67.95, 25.4) * mm, "end": v(-67.95, 22.47) * mm});
            skLineSegment(sketch, "E29.right", {"start": v(67.95, 25.4) * mm, "end": v(67.95, 22.47) * mm});
            skLineSegment(sketch, "E30.bottom", {"start": v(-67.95, 24.63) * mm, "end": v(67.95, 24.63) * mm});
            skLineSegment(sketch, "E30.top", {"start": v(-67.95, 23.17) * mm, "end": v(67.95, 23.17) * mm});
            skLineSegment(sketch, "E30.left", {"start": v(-67.95, 24.63) * mm, "end": v(-67.95, 23.17) * mm});
            skLineSegment(sketch, "E30.right", {"start": v(67.95, 24.63) * mm, "end": v(67.95, 23.17) * mm});
            skPoint(sketch, "E30.middle", {"position": v(0, 23.9) * mm});
            skPoint(sketch, "E30.middle.positionSnap0", {"position": v(0, 25.4) * mm});
            skPoint(sketch, "E30.centerSnap0", {"position": v(0, 25.4) * mm});
            skLineSegment(sketch, "E31.bottom", {"start": v(-67.95, -23.49) * mm, "end": v(67.95, -23.49) * mm});
            skLineSegment(sketch, "E31.top", {"start": v(-67.95, -24.95) * mm, "end": v(67.95, -24.95) * mm});
            skLineSegment(sketch, "E31.left", {"start": v(-67.95, -23.49) * mm, "end": v(-67.95, -24.95) * mm});
            skLineSegment(sketch, "E31.right", {"start": v(67.95, -23.49) * mm, "end": v(67.95, -24.95) * mm});
            skPoint(sketch, "E31.middle", {"position": v(0, -24.22) * mm});
            skSolve(sketch);
        }
        {
            var Q0;
            {var subQ0=sQuery(id+"F13.wireOp",EDGE,"E30.bottom");Q0=makeQuery(id+"F13.imprint","IMPRINT",FACE,{"disambiguationData":[TD([[makeQuery(id+"F13.imprint","IMPRINT",EDGE,{"derivedFrom":subQ0}),-1.0]])]});}
            var Q1;
            Q1=makeQuery(id+"F13.imprint","IMPRINT",FACE,{"disambiguationData":[TD([[makeQuery(id+"F13.imprint","IMPRINT",EDGE,{"derivedFrom":sQuery(id+"F13.wireOp",EDGE,"E28.bottom")}),-1.0]])]});
            var Q2;
            Q2=makeQuery(id+"F13.imprint","IMPRINT",FACE,{"disambiguationData":[TD([[makeQuery(id+"F13.imprint","IMPRINT",EDGE,{"derivedFrom":sQuery(id+"F13.wireOp",EDGE,"E31.bottom")}),-1.0]])]});
            extrude(context, id + "F14", {"entities" : qUnion([Q0, Q1, Q2]), "depth" : 2.92 * mm, "offsetDistance" : 25.4 * mm});
        }
        {
            var Q0;
            {var subQ0=sQuery(id+"F4.wireOp",EDGE,"E6.left");var subQ1=sQuery(id+"F4.wireOp",EDGE,"E6.top");var subQ2=sQuery(id+"F4.wireOp",EDGE,"E7.filletArc");var subQ3=sQuery(id+"F4.wireOp",EDGE,"E6.bottom");var subQ4=sQuery(id+"F4.wireOp",EDGE,"E10.filletArc");Q0=makeQuery(id+"F7.boolean.opBoolean","SPLIT",FACE,{"disambiguationData":[TD([makeQuery(id+"F5.boolean.opBoolean","COPY",FACE,{"derivedFrom":makeQuery(id+"F5.opExtrude","SWEPT_FACE",FACE,{"disambiguationData":[OSD([subQ0])]})})])],"derivedFrom":makeQuery(id+"F5.boolean.opBoolean","COPY",FACE,{"derivedFrom":makeQuery(id+"F5.opExtrude","CAP_FACE",FACE,{"disambiguationData":[OSD([subQ3,subQ1,subQ0,sQuery(id+"F4.wireOp",EDGE,"E6.right"),subQ2,sQuery(id+"F4.wireOp",EDGE,"E8.filletArc"),sQuery(id+"F4.wireOp",EDGE,"E9.filletArc"),subQ4])],"isStart":false})})});}
            var Q1;
            {var subQ0=sQuery(id+"F4.wireOp",EDGE,"E8.filletArc");var subQ1=sQuery(id+"F4.wireOp",EDGE,"E6.right");var subQ2=sQuery(id+"F4.wireOp",EDGE,"E6.top");var subQ3=sQuery(id+"F4.wireOp",EDGE,"E6.bottom");var subQ4=sQuery(id+"F4.wireOp",EDGE,"E9.filletArc");Q1=makeQuery(id+"F7.boolean.opBoolean","SPLIT",FACE,{"disambiguationData":[TD([makeQuery(id+"F5.boolean.opBoolean","COPY",FACE,{"derivedFrom":makeQuery(id+"F5.opExtrude","SWEPT_FACE",FACE,{"disambiguationData":[OSD([subQ1])]})})])],"derivedFrom":makeQuery(id+"F5.boolean.opBoolean","COPY",FACE,{"derivedFrom":makeQuery(id+"F5.opExtrude","CAP_FACE",FACE,{"disambiguationData":[OSD([subQ3,subQ2,sQuery(id+"F4.wireOp",EDGE,"E6.left"),subQ1,sQuery(id+"F4.wireOp",EDGE,"E7.filletArc"),subQ0,subQ4,sQuery(id+"F4.wireOp",EDGE,"E10.filletArc")])],"isStart":false})})});}
            extrude(context, id + "F15", {"entities" : qUnion([Q0, Q1]), "depth" : 2.92 * mm, "offsetDistance" : 25.4 * mm});
        }
    });
